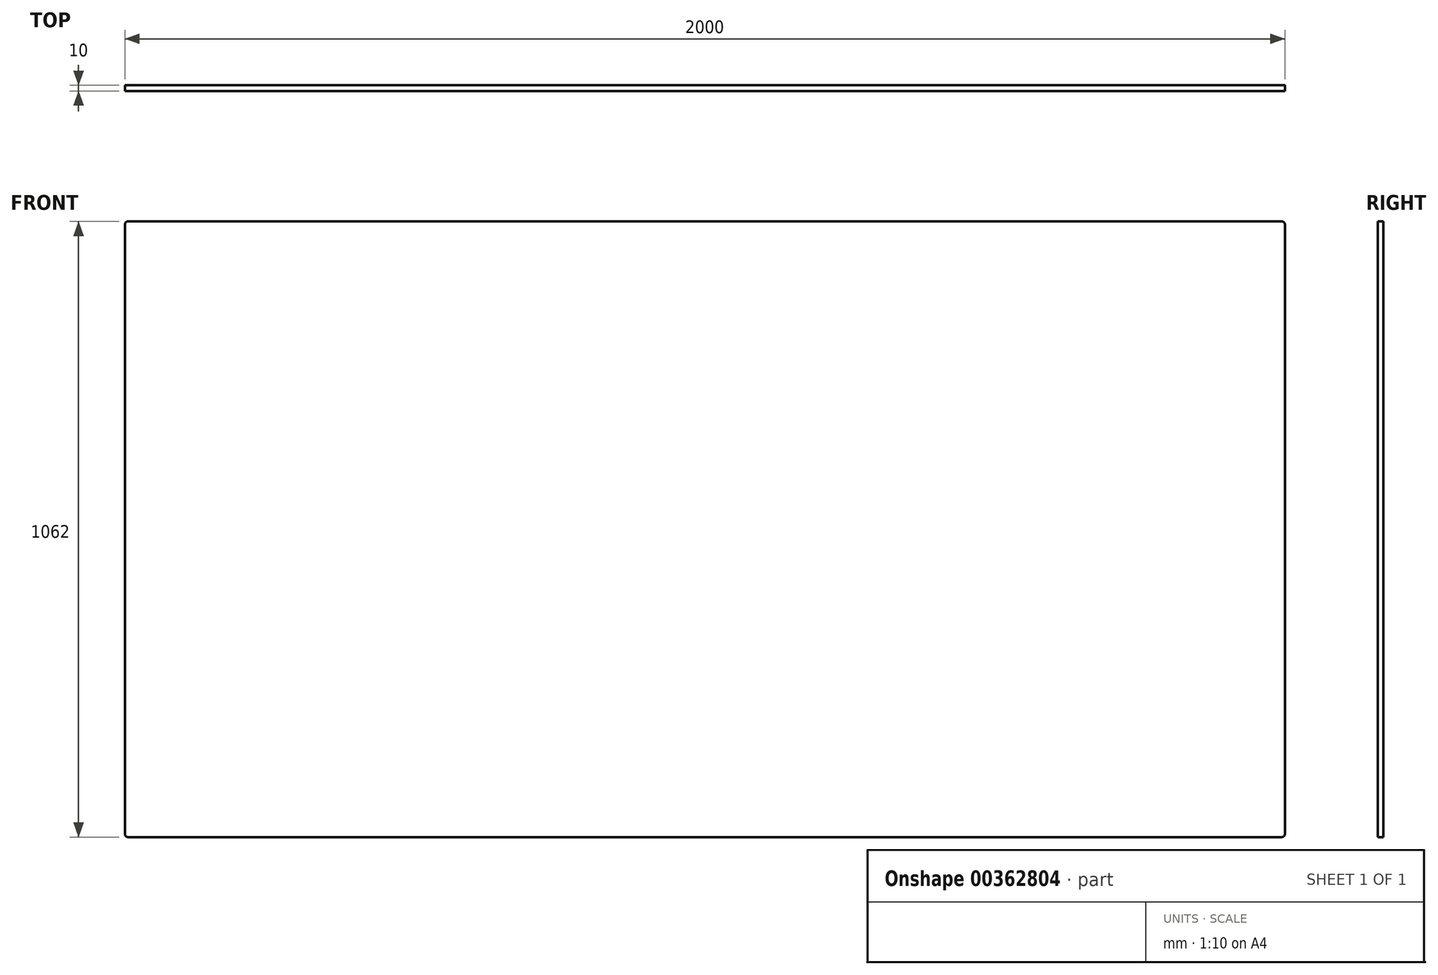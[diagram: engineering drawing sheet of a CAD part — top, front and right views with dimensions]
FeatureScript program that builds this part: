
annotation { "Feature Type Name" : "Feature", "Feature Type Description" : "" }
export const myFeature = defineFeature(function(context is Context, id is Id, definition is map)
    precondition{}
    {
        {
            var Q0;
            Q0=qCreatedBy(makeId("Front.planeOp"),FACE);
            var sketch = newSketch(context, id + "F0", { "sketchPlane" : qUnion([Q0])});
            skLineSegment(sketch, "E0.bottom", {"start": v(1000, 531) * mm, "end": v(-1000, 531) * mm});
            skLineSegment(sketch, "E0.top", {"start": v(1000, -531) * mm, "end": v(-1000, -531) * mm});
            skLineSegment(sketch, "E0.left", {"start": v(1000, 531) * mm, "end": v(1000, -531) * mm});
            skLineSegment(sketch, "E0.right", {"start": v(-1000, 531) * mm, "end": v(-1000, -531) * mm});
            skPoint(sketch, "E0.middle", {"position": v(0, 0) * mm});
            skSolve(sketch);
        }
        {
            var Q0;
            Q0=makeQuery(id+"F0.imprint","IMPRINT",FACE,{"disambiguationData":[TD([[makeQuery(id+"F0.imprint","IMPRINT",EDGE,{"derivedFrom":sQuery(id+"F0.wireOp",EDGE,"E0.bottom")}),1.0]])]});
            extrude(context, id + "F1", {"entities" : qUnion([Q0]), "depth" : 10 * mm});
        }
        {
            var Q0;
            Q0=makeQuery(id+"F1.opExtrude","SWEPT_EDGE",EDGE,{"disambiguationData":[OSD([sQuery(id+"F0.wireOp",EDGE,"E0.bottom"),sQuery(id+"F0.wireOp",EDGE,"E0.right")])]});
            var Q1;
            Q1=makeQuery(id+"F1.opExtrude","SWEPT_EDGE",EDGE,{"disambiguationData":[OSD([sQuery(id+"F0.wireOp",EDGE,"E0.top"),sQuery(id+"F0.wireOp",EDGE,"E0.right")])]});
            var Q2;
            Q2=makeQuery(id+"F1.opExtrude","SWEPT_EDGE",EDGE,{"disambiguationData":[OSD([sQuery(id+"F0.wireOp",EDGE,"E0.top"),sQuery(id+"F0.wireOp",EDGE,"E0.left")])]});
            var Q3;
            Q3=makeQuery(id+"F1.opExtrude","SWEPT_EDGE",EDGE,{"disambiguationData":[OSD([sQuery(id+"F0.wireOp",EDGE,"E0.bottom"),sQuery(id+"F0.wireOp",EDGE,"E0.left")])]});
            fillet(context, id + "F2", {"entities" : qUnion([Q0, Q1, Q2, Q3]), "radius" : 5 * mm, "tangentPropagation" : true, "allowEdgeOverflow" : false});
        }
    });
